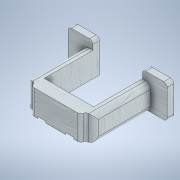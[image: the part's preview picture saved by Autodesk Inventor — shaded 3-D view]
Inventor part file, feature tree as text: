
AUTODESK INVENTOR PART (.ipt)
format: ipt  version: 2021 (Build 250183000, 183)  size: 214,016 bytes
history: native  units: mm
features: extrude x6, sketch x6, fillet x3
ambient origin geometry x8: Origin, YZ Plane, XZ Plane, XY Plane, X Axis, Y Axis, Z Axis, Center Point
bodies: Solid1 (feature_tree)
feature tree (15):
  extrude  "Extrusion1"  Depth=15.0mm
  extrude  "Extrusion2"  Depth=30.0mm
  fillet  "Fillet1"  Radius=15.0mm
  extrude  "Extrusion3"  Depth=3.0mm TaperAngle=0.0deg
  extrude  "Extrusion4"  Depth=5.0mm
  fillet  "Fillet2"  Radius=5.0mm
  fillet  "Fillet3"  Radius=33.5mm
  extrude  "Extrusion5"  Depth=20.0mm
  extrude  "Extrusion6"  Depth=4.0mm TaperAngle=0.0deg
  sketch  "Sketch1"  dims[d0=40.0mm d1=15.0mm]
  sketch  "Sketch2"  dims[d2=5.0mm d3=0.0mm d4=30.0mm d5=15.0mm]
  sketch  "Sketch3"  dims[d6=5.0mm d7=3.0mm d8=0.0mm]
  sketch  "Sketch4"  dims[d9=2.0mm d10=5.0mm d11=5.0mm d12=33.5mm d13=0.0mm]
  sketch  "Sketch5"  dims[d18=15.0mm d19=20.0mm]
  sketch  "Sketch6"  dims[d20=15.0mm d21=4.0mm d22=0.0mm d23=3.0mm d24=2.0mm d25=1.0mm d26=0.0mm d27=1.5mm d28=1.5mm d29=10.0mm d30=0.0mm]
